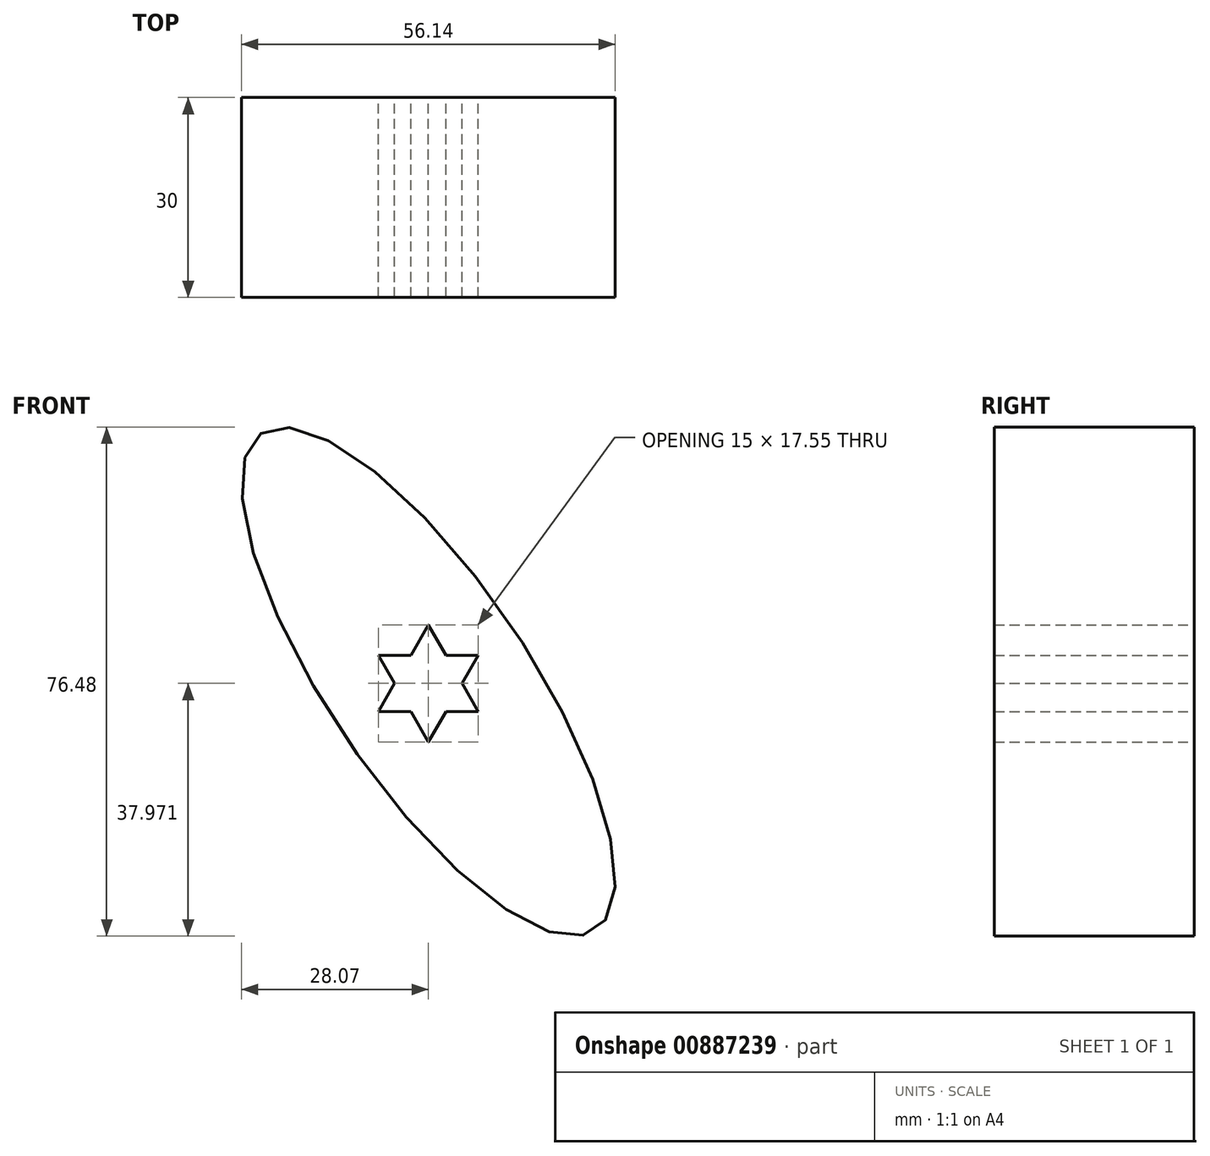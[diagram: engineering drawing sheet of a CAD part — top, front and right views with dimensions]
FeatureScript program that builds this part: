
annotation { "Feature Type Name" : "Feature", "Feature Type Description" : "" }
export const myFeature = defineFeature(function(context is Context, id is Id, definition is map)
    precondition{}
    {
        {
            var Q0;
            Q0=qCreatedBy(makeId("Front.planeOp"),FACE);
            var sketch = newSketch(context, id + "F0", { "sketchPlane" : qUnion([Q0])});
            skEllipse(sketch, "E0", {"center": v(0, 0) * mm, "majorRadius": 15 * mm, "minorRadius": 45 * mm, "majorAxis": v(0.83, 0.56)});
            skSolve(sketch);
        }
        {
            var Q0;
            Q0 = qSketchRegion(id + "F0", true);
            extrude(context, id + "F1", {"entities" : qUnion([Q0]), "depth" : 30 * mm, "offsetDistance" : 25 * mm});
        }
        {
            var Q0;
            Q0=makeQuery(id+"F1.opExtrude","CAP_FACE",FACE,{"disambiguationData":[OSD([sQuery(id+"F0.wireOp",EDGE,"E0")])],"isStart":true});
            var sketch = newSketch(context, id + "F2", { "sketchPlane" : qUnion([Q0])});
            skLineSegment(sketch, "E1", {"start": v(-7.5, 3.95) * mm, "end": v(7.5, 3.95) * mm});
            skLineSegment(sketch, "E2", {"start": v(7.5, 3.95) * mm, "end": v(0, -9.04) * mm});
            skPoint(sketch, "E2.endSnap0", {"position": v(0, 3.95) * mm});
            skLineSegment(sketch, "E3", {"start": v(0, -9.04) * mm, "end": v(-7.5, 3.95) * mm});
            skLineSegment(sketch, "E4", {"start": v(-7.5, -4.49) * mm, "end": v(7.5, -4.49) * mm});
            skLineSegment(sketch, "E5", {"start": v(7.5, -4.49) * mm, "end": v(0, 8.5) * mm});
            skLineSegment(sketch, "E6", {"start": v(0, 8.5) * mm, "end": v(-7.5, -4.49) * mm});
            skSolve(sketch);
        }
        {
            var Q0;
            Q0 = qSketchRegion(id + "F2", true);
            extrude(context, id + "F3", {"entities" : qUnion([Q0]), "operationType" : NewBodyOperationType.REMOVE, "endBound" : BoundingType.THROUGH_ALL, "oppositeDirection" : true, "depth" : 25 * mm, "offsetDistance" : 25 * mm});
        }
    });
